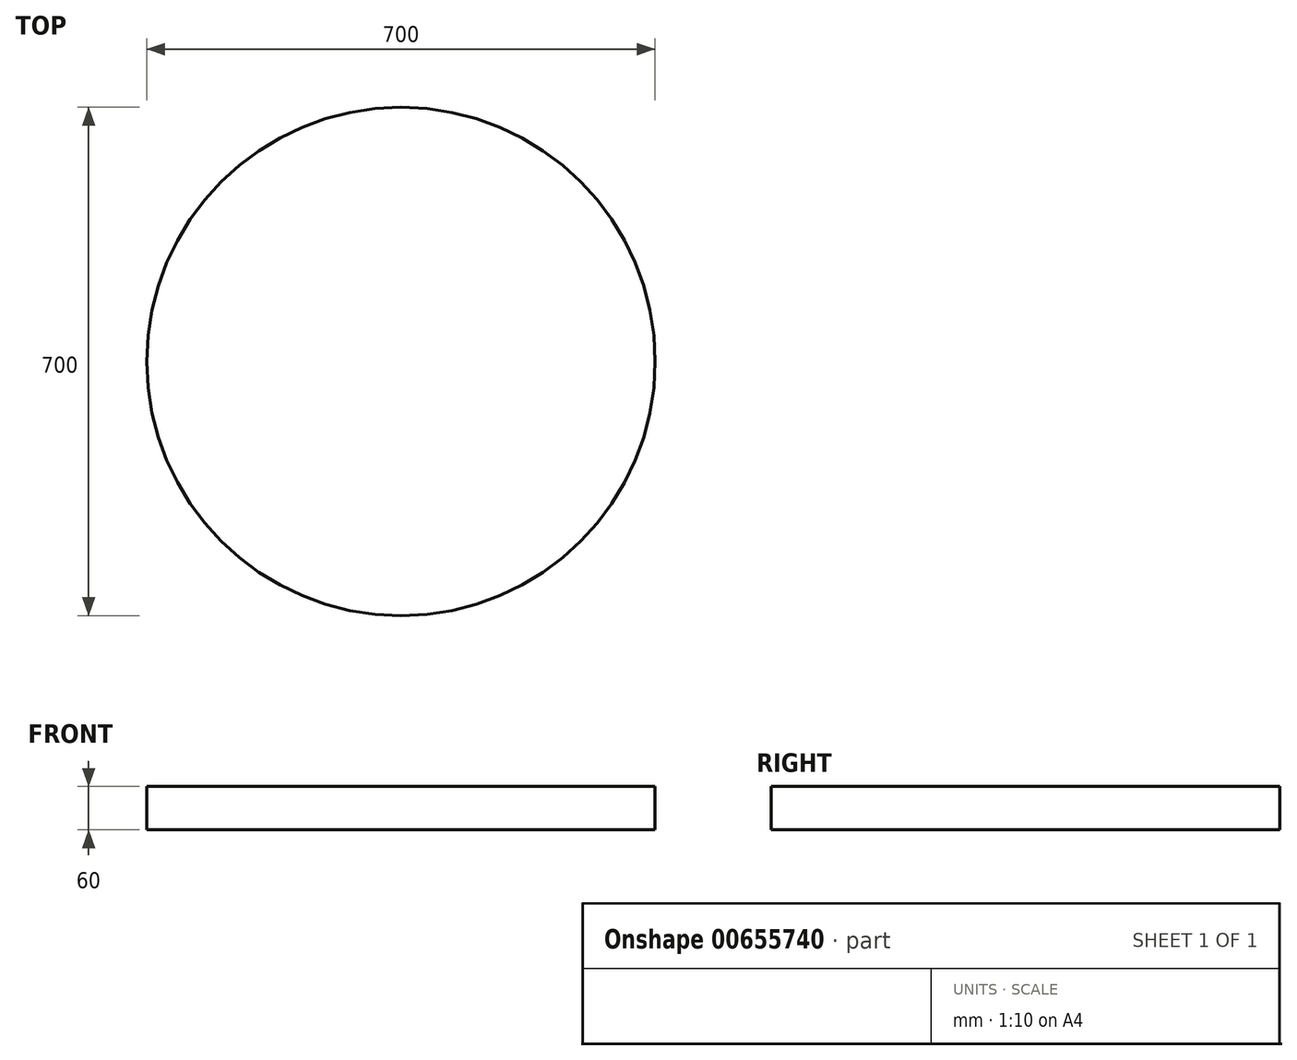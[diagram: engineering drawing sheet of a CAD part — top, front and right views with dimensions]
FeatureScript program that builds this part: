
annotation { "Feature Type Name" : "Feature", "Feature Type Description" : "" }
export const myFeature = defineFeature(function(context is Context, id is Id, definition is map)
    precondition{}
    {
        {
            var Q0;
            Q0=qCreatedBy(makeId("Top.planeOp"),FACE);
            var sketch = newSketch(context, id + "F0", { "sketchPlane" : qUnion([Q0])});
            skCircle(sketch, "E0", {"center": v(0, 0) * mm, "radius": 350 * mm});
            skSolve(sketch);
        }
        {
            var Q0;
            Q0=makeQuery(id+"F0.imprint","IMPRINT",FACE,{"disambiguationData":[TD([[makeQuery(id+"F0.imprint","IMPRINT",EDGE,{"derivedFrom":sQuery(id+"F0.wireOp",EDGE,"E0")}),1.0]])]});
            extrude(context, id + "F1", {"entities" : qUnion([Q0]), "depth" : 60 * mm, "offsetDistance" : 25.4 * mm});
        }
    });
